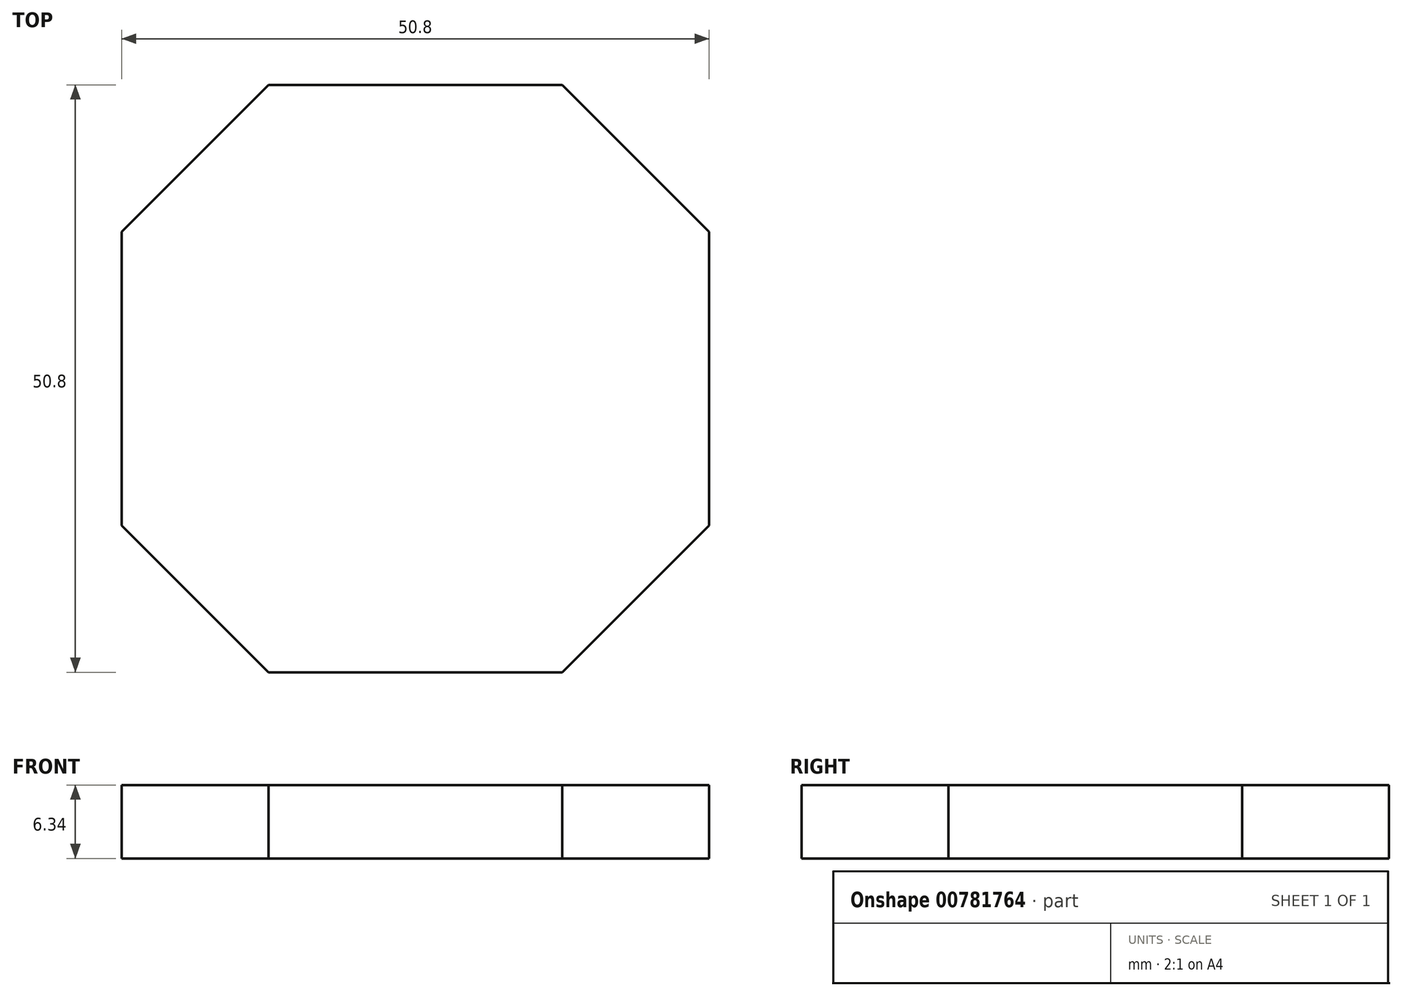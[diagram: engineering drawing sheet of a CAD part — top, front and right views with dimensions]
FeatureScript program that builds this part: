
annotation { "Feature Type Name" : "Feature", "Feature Type Description" : "" }
export const myFeature = defineFeature(function(context is Context, id is Id, definition is map)
    precondition{}
    {
        {
            var Q0;
            Q0=qCreatedBy(makeId("Top.planeOp"),FACE);
            var sketch = newSketch(context, id + "F0", { "sketchPlane" : qUnion([Q0])});
            skLineSegment(sketch, "E0.bottom", {"start": v(25.4, -25.4) * mm, "end": v(-25.4, -25.4) * mm});
            skLineSegment(sketch, "E0.top", {"start": v(25.4, 25.4) * mm, "end": v(-25.4, 25.4) * mm});
            skLineSegment(sketch, "E0.left", {"start": v(25.4, -25.4) * mm, "end": v(25.4, 25.4) * mm});
            skLineSegment(sketch, "E0.right", {"start": v(-25.4, -25.4) * mm, "end": v(-25.4, 25.4) * mm});
            skPoint(sketch, "E0.middle", {"position": v(0, 0) * mm});
            skSolve(sketch);
        }
        {
            var Q0;
            Q0 = qSketchRegion(id + "F0", true);
            extrude(context, id + "F1", {"entities" : qUnion([Q0]), "endBound" : BoundingType.SYMMETRIC, "depth" : 6.35 * mm, "offsetDistance" : 25.4 * mm});
        }
        {
            var Q0;
            Q0=makeQuery(id+"F1.opExtrude","SWEPT_EDGE",EDGE,{"disambiguationData":[OSD([sQuery(id+"F0.wireOp",EDGE,"E0.bottom"),sQuery(id+"F0.wireOp",EDGE,"E0.right")])]});
            var Q1;
            Q1=makeQuery(id+"F1.opExtrude","SWEPT_EDGE",EDGE,{"disambiguationData":[OSD([sQuery(id+"F0.wireOp",EDGE,"E0.bottom"),sQuery(id+"F0.wireOp",EDGE,"E0.left")])]});
            var Q2;
            Q2=makeQuery(id+"F1.opExtrude","SWEPT_EDGE",EDGE,{"disambiguationData":[OSD([sQuery(id+"F0.wireOp",EDGE,"E0.top"),sQuery(id+"F0.wireOp",EDGE,"E0.left")])]});
            var Q3;
            Q3=makeQuery(id+"F1.opExtrude","SWEPT_EDGE",EDGE,{"disambiguationData":[OSD([sQuery(id+"F0.wireOp",EDGE,"E0.top"),sQuery(id+"F0.wireOp",EDGE,"E0.right")])]});
            chamfer(context, id + "F2", {"entities" : qUnion([Q0, Q1, Q2, Q3]), "width" : 12.7 * mm, "tangentPropagation" : true});
        }
    });
